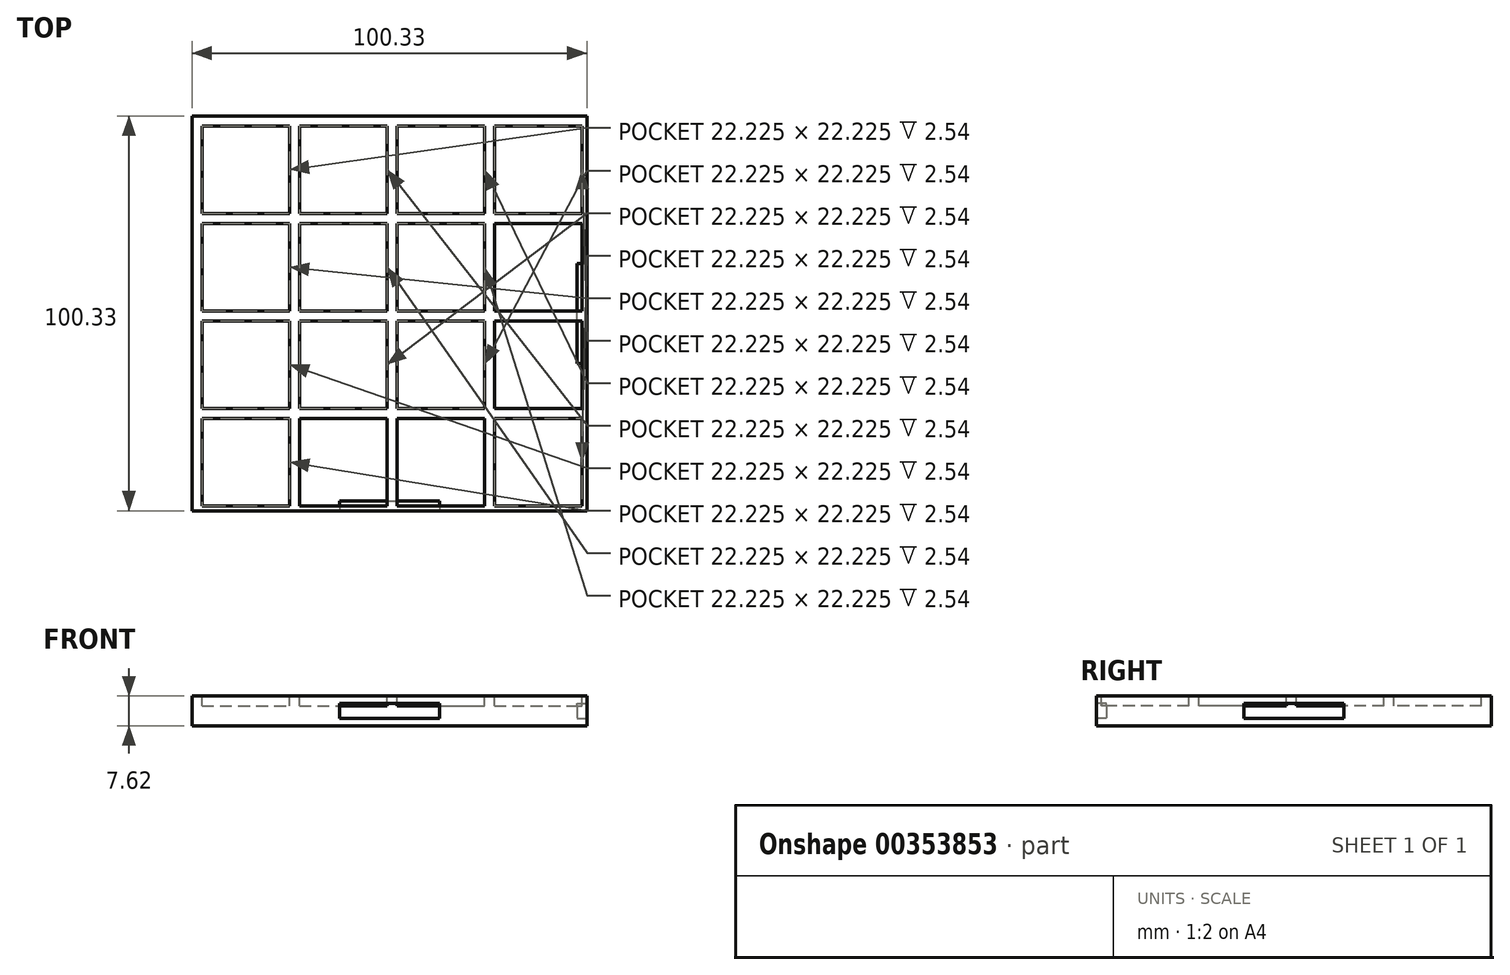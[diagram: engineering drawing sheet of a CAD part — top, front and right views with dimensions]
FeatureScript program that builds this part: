
annotation { "Feature Type Name" : "Feature", "Feature Type Description" : "" }
export const myFeature = defineFeature(function(context is Context, id is Id, definition is map)
    precondition{}
    {
        {
            var Q0;
            Q0=qCreatedBy(makeId("Top.planeOp"),FACE);
            var sketch = newSketch(context, id + "F0", { "sketchPlane" : qUnion([Q0])});
            skLineSegment(sketch, "E0.bottom", {"start": v(0, 0) * mm, "end": v(100.33, 0) * mm});
            skLineSegment(sketch, "E0.top", {"start": v(0, 100.33) * mm, "end": v(100.33, 100.33) * mm});
            skLineSegment(sketch, "E0.left", {"start": v(0, 0) * mm, "end": v(0, 100.33) * mm});
            skLineSegment(sketch, "E0.right", {"start": v(100.33, 0) * mm, "end": v(100.33, 100.33) * mm});
            skSolve(sketch);
        }
        {
            var Q0;
            Q0=qSketchRegion(id+"F0",true);
            extrude(context, id + "F1", {"entities" : qUnion([Q0]), "oppositeDirection" : true, "depth" : 7.62 * mm});
        }
        {
            var Q0;
            Q0=qCreatedBy(makeId("Top.planeOp"),FACE);
            var sketch = newSketch(context, id + "F2", { "sketchPlane" : qUnion([Q0])});
            skLineSegment(sketch, "E1.bottom", {"start": v(2.54, 97.8) * mm, "end": v(24.77, 97.8) * mm});
            skLineSegment(sketch, "E1.top", {"start": v(2.54, 75.57) * mm, "end": v(24.77, 75.57) * mm});
            skLineSegment(sketch, "E1.left", {"start": v(2.54, 97.8) * mm, "end": v(2.54, 75.57) * mm});
            skLineSegment(sketch, "E1.right", {"start": v(24.77, 97.8) * mm, "end": v(24.77, 75.56) * mm});
            skLineSegment(sketch, "E2.bottom", {"start": v(27.3, 97.8) * mm, "end": v(49.53, 97.8) * mm});
            skLineSegment(sketch, "E2.top", {"start": v(27.3, 75.56) * mm, "end": v(49.53, 75.57) * mm});
            skLineSegment(sketch, "E2.left", {"start": v(27.3, 97.8) * mm, "end": v(27.3, 75.56) * mm});
            skLineSegment(sketch, "E2.right", {"start": v(49.53, 97.8) * mm, "end": v(49.53, 75.56) * mm});
            skLineSegment(sketch, "E3.bottom", {"start": v(52.07, 97.8) * mm, "end": v(74.3, 97.8) * mm});
            skLineSegment(sketch, "E3.top", {"start": v(52.07, 75.57) * mm, "end": v(74.3, 75.57) * mm});
            skLineSegment(sketch, "E3.left", {"start": v(52.07, 97.8) * mm, "end": v(52.07, 75.57) * mm});
            skLineSegment(sketch, "E3.right", {"start": v(74.3, 97.8) * mm, "end": v(74.3, 75.57) * mm});
            skLineSegment(sketch, "E4.bottom", {"start": v(76.84, 97.8) * mm, "end": v(99.06, 97.8) * mm});
            skLineSegment(sketch, "E4.top", {"start": v(76.84, 75.57) * mm, "end": v(99.06, 75.56) * mm});
            skLineSegment(sketch, "E4.left", {"start": v(76.84, 97.8) * mm, "end": v(76.84, 75.57) * mm});
            skLineSegment(sketch, "E4.right", {"start": v(99.06, 97.8) * mm, "end": v(99.06, 75.57) * mm});
            skLineSegment(sketch, "E5.bottom", {"start": v(2.54, 73.03) * mm, "end": v(24.77, 73.03) * mm});
            skLineSegment(sketch, "E5.top", {"start": v(2.54, 50.8) * mm, "end": v(24.76, 50.8) * mm});
            skLineSegment(sketch, "E5.left", {"start": v(2.54, 73.03) * mm, "end": v(2.54, 50.8) * mm});
            skLineSegment(sketch, "E5.right", {"start": v(24.76, 73.03) * mm, "end": v(24.76, 50.8) * mm});
            skLineSegment(sketch, "E6.bottom", {"start": v(2.54, 48.26) * mm, "end": v(24.77, 48.26) * mm});
            skLineSegment(sketch, "E6.top", {"start": v(2.54, 26.04) * mm, "end": v(24.77, 26.04) * mm});
            skLineSegment(sketch, "E6.left", {"start": v(2.54, 48.26) * mm, "end": v(2.54, 26.04) * mm});
            skLineSegment(sketch, "E6.right", {"start": v(24.77, 48.26) * mm, "end": v(24.77, 26.04) * mm});
            skLineSegment(sketch, "E7.bottom", {"start": v(2.54, 23.5) * mm, "end": v(24.77, 23.5) * mm});
            skLineSegment(sketch, "E7.top", {"start": v(2.54, 1.27) * mm, "end": v(24.76, 1.27) * mm});
            skLineSegment(sketch, "E7.left", {"start": v(2.54, 23.5) * mm, "end": v(2.54, 1.27) * mm});
            skLineSegment(sketch, "E7.right", {"start": v(24.77, 23.5) * mm, "end": v(24.77, 1.27) * mm});
            skLineSegment(sketch, "E8.bottom", {"start": v(27.3, 73.02) * mm, "end": v(49.53, 73.02) * mm});
            skLineSegment(sketch, "E8.top", {"start": v(27.3, 50.8) * mm, "end": v(49.53, 50.8) * mm});
            skLineSegment(sketch, "E8.left", {"start": v(27.3, 73.02) * mm, "end": v(27.3, 50.8) * mm});
            skLineSegment(sketch, "E8.right", {"start": v(49.53, 73.02) * mm, "end": v(49.53, 50.8) * mm});
            skLineSegment(sketch, "E9.bottom", {"start": v(52.07, 73.03) * mm, "end": v(74.3, 73.03) * mm});
            skLineSegment(sketch, "E9.top", {"start": v(52.07, 50.8) * mm, "end": v(74.3, 50.8) * mm});
            skLineSegment(sketch, "E9.left", {"start": v(52.07, 73.03) * mm, "end": v(52.07, 50.8) * mm});
            skLineSegment(sketch, "E9.right", {"start": v(74.3, 73.03) * mm, "end": v(74.3, 50.8) * mm});
            skLineSegment(sketch, "E10.bottom", {"start": v(76.83, 73.03) * mm, "end": v(99.06, 73.03) * mm});
            skLineSegment(sketch, "E10.top", {"start": v(76.83, 50.8) * mm, "end": v(99.06, 50.8) * mm});
            skLineSegment(sketch, "E10.left", {"start": v(76.83, 73.03) * mm, "end": v(76.83, 50.8) * mm});
            skLineSegment(sketch, "E10.right", {"start": v(99.06, 73.03) * mm, "end": v(99.06, 50.8) * mm});
            skLineSegment(sketch, "E11.bottom", {"start": v(27.3, 48.26) * mm, "end": v(49.53, 48.26) * mm});
            skLineSegment(sketch, "E11.top", {"start": v(27.3, 26.03) * mm, "end": v(49.53, 26.03) * mm});
            skLineSegment(sketch, "E11.left", {"start": v(27.3, 48.26) * mm, "end": v(27.3, 26.03) * mm});
            skLineSegment(sketch, "E11.right", {"start": v(49.53, 48.26) * mm, "end": v(49.53, 26.03) * mm});
            skLineSegment(sketch, "E12.bottom", {"start": v(27.3, 23.5) * mm, "end": v(49.53, 23.5) * mm});
            skLineSegment(sketch, "E12.top", {"start": v(27.3, 1.27) * mm, "end": v(49.53, 1.27) * mm});
            skLineSegment(sketch, "E12.left", {"start": v(27.3, 23.5) * mm, "end": v(27.3, 1.27) * mm});
            skLineSegment(sketch, "E12.right", {"start": v(49.53, 23.5) * mm, "end": v(49.53, 1.27) * mm});
            skLineSegment(sketch, "E13.bottom", {"start": v(52.07, 48.26) * mm, "end": v(74.3, 48.26) * mm});
            skLineSegment(sketch, "E13.top", {"start": v(52.07, 26.03) * mm, "end": v(74.3, 26.03) * mm});
            skLineSegment(sketch, "E13.left", {"start": v(52.07, 48.26) * mm, "end": v(52.07, 26.03) * mm});
            skLineSegment(sketch, "E13.right", {"start": v(74.3, 48.26) * mm, "end": v(74.3, 26.03) * mm});
            skLineSegment(sketch, "E14.bottom", {"start": v(76.84, 48.26) * mm, "end": v(99.06, 48.26) * mm});
            skLineSegment(sketch, "E14.top", {"start": v(76.84, 26.04) * mm, "end": v(99.06, 26.03) * mm});
            skLineSegment(sketch, "E14.left", {"start": v(76.84, 48.26) * mm, "end": v(76.84, 26.04) * mm});
            skLineSegment(sketch, "E14.right", {"start": v(99.06, 48.26) * mm, "end": v(99.06, 26.03) * mm});
            skLineSegment(sketch, "E15.bottom", {"start": v(52.07, 23.5) * mm, "end": v(74.3, 23.5) * mm});
            skLineSegment(sketch, "E15.top", {"start": v(52.07, 1.27) * mm, "end": v(74.3, 1.27) * mm});
            skLineSegment(sketch, "E15.left", {"start": v(52.07, 23.5) * mm, "end": v(52.07, 1.27) * mm});
            skLineSegment(sketch, "E15.right", {"start": v(74.3, 23.5) * mm, "end": v(74.3, 1.27) * mm});
            skLineSegment(sketch, "E16.bottom", {"start": v(76.84, 23.5) * mm, "end": v(99.06, 23.5) * mm});
            skLineSegment(sketch, "E16.top", {"start": v(76.84, 1.27) * mm, "end": v(99.06, 1.27) * mm});
            skLineSegment(sketch, "E16.left", {"start": v(76.84, 23.5) * mm, "end": v(76.84, 1.27) * mm});
            skLineSegment(sketch, "E16.right", {"start": v(99.06, 23.5) * mm, "end": v(99.06, 1.27) * mm});
            skSolve(sketch);
        }
        {
            var Q0;
            Q0=qSketchRegion(id+"F2",true);
            extrude(context, id + "F3", {"entities" : qUnion([Q0]), "operationType" : NewBodyOperationType.REMOVE, "oppositeDirection" : true, "depth" : 2.54 * mm});
        }
        {
            var Q0;
            Q0=makeQuery(id+"F1.opExtrude","SWEPT_FACE",FACE,{"disambiguationData":[OSD([sQuery(id+"F0.wireOp",EDGE,"E0.bottom")])]});
            var sketch = newSketch(context, id + "F4", { "sketchPlane" : qUnion([Q0])});
            skLineSegment(sketch, "E17.bottom", {"start": v(37.47, -1.9) * mm, "end": v(62.87, -1.9) * mm});
            skLineSegment(sketch, "E17.top", {"start": v(37.47, -5.71) * mm, "end": v(62.87, -5.71) * mm});
            skLineSegment(sketch, "E17.left", {"start": v(37.47, -1.9) * mm, "end": v(37.47, -5.71) * mm});
            skLineSegment(sketch, "E17.right", {"start": v(62.87, -1.9) * mm, "end": v(62.87, -5.71) * mm});
            skLineSegment(sketch, "E18", {"start": v(37.47, -1.9) * mm, "end": v(0, -1.9) * mm, "construction": true});
            skLineSegment(sketch, "E19", {"start": v(62.87, -3.8) * mm, "end": v(100.33, -3.8) * mm, "construction": true});
            skLineSegment(sketch, "E20", {"start": v(52.96, -1.9) * mm, "end": v(52.96, 0) * mm, "construction": true});
            skLineSegment(sketch, "E21", {"start": v(54.09, -5.71) * mm, "end": v(54.09, -7.62) * mm, "construction": true});
            skSolve(sketch);
        }
        {
            var Q0;
            Q0=makeQuery(id+"F1.opExtrude","SWEPT_FACE",FACE,{"disambiguationData":[OSD([sQuery(id+"F0.wireOp",EDGE,"E0.right")])]});
            var sketch = newSketch(context, id + "F5", { "sketchPlane" : qUnion([Q0])});
            skLineSegment(sketch, "E22.bottom", {"start": v(37.46, -1.9) * mm, "end": v(62.86, -1.9) * mm});
            skLineSegment(sketch, "E22.top", {"start": v(37.46, -5.71) * mm, "end": v(62.86, -5.71) * mm});
            skLineSegment(sketch, "E22.left", {"start": v(37.46, -1.9) * mm, "end": v(37.46, -5.71) * mm});
            skLineSegment(sketch, "E22.right", {"start": v(62.86, -1.9) * mm, "end": v(62.86, -5.71) * mm});
            skLineSegment(sketch, "E23", {"start": v(0, -3.81) * mm, "end": v(37.46, -3.81) * mm, "construction": true});
            skLineSegment(sketch, "E24", {"start": v(62.86, -3.81) * mm, "end": v(100.33, -3.81) * mm, "construction": true});
            skLineSegment(sketch, "E25", {"start": v(47.77, -5.71) * mm, "end": v(47.77, -7.62) * mm, "construction": true});
            skPoint(sketch, "E25.endSnap0", {"position": v(50.16, -7.62) * mm});
            skLineSegment(sketch, "E26", {"start": v(48.6, -1.9) * mm, "end": v(48.6, 0) * mm, "construction": true});
            skSolve(sketch);
        }
        {
            var Q0;
            Q0=makeQuery(id+"F4.imprint","IMPRINT",FACE,{"disambiguationData":[TD([[makeQuery(id+"F4.imprint","IMPRINT",EDGE,{"derivedFrom":sQuery(id+"F4.wireOp",EDGE,"E17.bottom")}),-1.0]])]});
            extrude(context, id + "F6", {"entities" : qUnion([Q0]), "operationType" : NewBodyOperationType.REMOVE, "oppositeDirection" : true, "depth" : 2.54 * mm});
        }
        {
            var Q0;
            Q0=makeQuery(id+"F5.imprint","IMPRINT",FACE,{"disambiguationData":[TD([[makeQuery(id+"F5.imprint","IMPRINT",EDGE,{"derivedFrom":sQuery(id+"F5.wireOp",EDGE,"E22.bottom")}),-1.0]])]});
            extrude(context, id + "F7", {"entities" : qUnion([Q0]), "operationType" : NewBodyOperationType.REMOVE, "oppositeDirection" : true, "depth" : 2.54 * mm});
        }
    });
